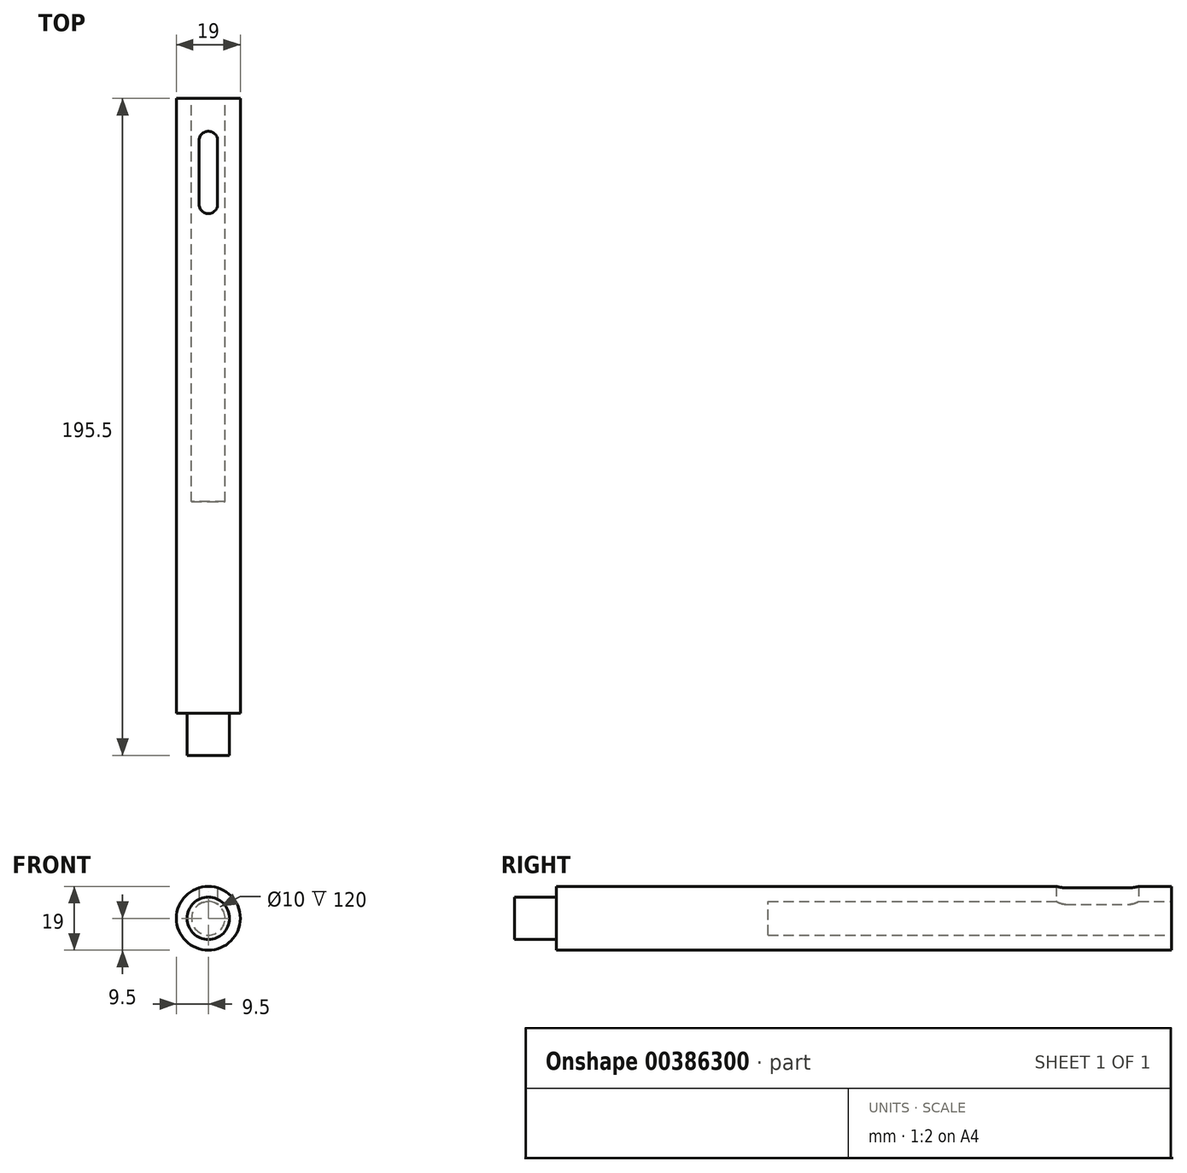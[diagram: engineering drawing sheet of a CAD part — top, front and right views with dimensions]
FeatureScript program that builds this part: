
annotation { "Feature Type Name" : "Feature", "Feature Type Description" : "" }
export const myFeature = defineFeature(function(context is Context, id is Id, definition is map)
    precondition{}
    {
        {
            var Q0;
            Q0=qCreatedBy(makeId("Front.planeOp"),FACE);
            var sketch = newSketch(context, id + "F0", { "sketchPlane" : qUnion([Q0])});
            skCircle(sketch, "E0", {"center": v(0, 0) * mm, "radius": 9.5 * mm});
            skCircle(sketch, "E1", {"center": v(0, 0) * mm, "radius": 5 * mm});
            skLineSegment(sketch, "E2", {"start": v(0, 20.65) * mm, "end": v(0, -19.38) * mm});
            skSolve(sketch);
        }
        {
            var Q0;
            {var subQ0=sQuery(id+"F0.wireOp",EDGE,"E2");var subQ1=sQuery(id+"F0.wireOp",EDGE,"E0");var subQ2=makeQuery(id+"F0.imprint","INTERSECT",VERTEX,{"disambiguationData":[OD(0.0)],"derivedFrom":[subQ1,subQ0]});Q0=makeQuery(id+"F0.imprint","IMPRINT",FACE,{"disambiguationData":[TD([[makeQuery(id+"F0.imprint","IMPRINT",EDGE,{"disambiguationData":[TD([[subQ2,-1.0]])],"derivedFrom":subQ1}),1.0]])]});}
            var Q1;
            {var subQ0=sQuery(id+"F0.wireOp",EDGE,"E2");var subQ1=sQuery(id+"F0.wireOp",EDGE,"E1");var subQ2=makeQuery(id+"F0.imprint","INTERSECT",VERTEX,{"disambiguationData":[OD(0.0)],"derivedFrom":[subQ1,subQ0]});Q1=makeQuery(id+"F0.imprint","IMPRINT",FACE,{"disambiguationData":[TD([[makeQuery(id+"F0.imprint","IMPRINT",EDGE,{"disambiguationData":[TD([[subQ2,-1.0]])],"derivedFrom":subQ1}),1.0]])]});}
            var Q2;
            {var subQ0=sQuery(id+"F0.wireOp",EDGE,"E2");var subQ1=sQuery(id+"F0.wireOp",EDGE,"E1");var subQ2=makeQuery(id+"F0.imprint","INTERSECT",VERTEX,{"disambiguationData":[OD(0.0)],"derivedFrom":[subQ1,subQ0]});Q2=makeQuery(id+"F0.imprint","IMPRINT",FACE,{"disambiguationData":[TD([[makeQuery(id+"F0.imprint","IMPRINT",EDGE,{"disambiguationData":[TD([[subQ2,1.0]])],"derivedFrom":subQ1}),1.0]])]});}
            var Q3;
            {var subQ0=sQuery(id+"F0.wireOp",EDGE,"E2");var subQ1=sQuery(id+"F0.wireOp",EDGE,"E0");var subQ2=makeQuery(id+"F0.imprint","INTERSECT",VERTEX,{"disambiguationData":[OD(0.0)],"derivedFrom":[subQ1,subQ0]});Q3=makeQuery(id+"F0.imprint","IMPRINT",FACE,{"disambiguationData":[TD([[makeQuery(id+"F0.imprint","IMPRINT",EDGE,{"disambiguationData":[TD([[subQ2,1.0]])],"derivedFrom":subQ1}),1.0]])]});}
            extrude(context, id + "F1", {"entities" : qUnion([Q0, Q1, Q2, Q3]), "depth" : 183 * mm});
        }
        {
            var Q0;
            {var subQ0=sQuery(id+"F0.wireOp",EDGE,"E2");var subQ1=sQuery(id+"F0.wireOp",EDGE,"E1");var subQ2=makeQuery(id+"F0.imprint","INTERSECT",VERTEX,{"disambiguationData":[OD(0.0)],"derivedFrom":[subQ1,subQ0]});Q0=makeQuery(id+"F0.imprint","IMPRINT",FACE,{"disambiguationData":[TD([[makeQuery(id+"F0.imprint","IMPRINT",EDGE,{"disambiguationData":[TD([[subQ2,-1.0]])],"derivedFrom":subQ1}),1.0]])]});}
            var Q1;
            {var subQ0=sQuery(id+"F0.wireOp",EDGE,"E2");var subQ1=sQuery(id+"F0.wireOp",EDGE,"E1");var subQ2=makeQuery(id+"F0.imprint","INTERSECT",VERTEX,{"disambiguationData":[OD(0.0)],"derivedFrom":[subQ1,subQ0]});Q1=makeQuery(id+"F0.imprint","IMPRINT",FACE,{"disambiguationData":[TD([[makeQuery(id+"F0.imprint","IMPRINT",EDGE,{"disambiguationData":[TD([[subQ2,1.0]])],"derivedFrom":subQ1}),1.0]])]});}
            extrude(context, id + "F2", {"entities" : qUnion([Q0, Q1]), "operationType" : NewBodyOperationType.REMOVE, "depth" : 120 * mm});
        }
        {
            var Q0;
            Q0=qCreatedBy(makeId("Top.planeOp"),FACE);
            var sketch = newSketch(context, id + "F3", { "sketchPlane" : qUnion([Q0])});
            skArc(sketch, "E3", {"start": v(2.75, -12.5) * mm, "mid": v(0, -9.75) * mm, "end": v(-2.75, -12.5) * mm});
            skArc(sketch, "E4", {"start": v(-2.75, -31.5) * mm, "mid": v(0, -34.25) * mm, "end": v(2.75, -31.5) * mm});
            skLineSegment(sketch, "E5", {"start": v(2.75, -12.5) * mm, "end": v(2.75, -31.5) * mm});
            skLineSegment(sketch, "E6", {"start": v(-2.75, -12.5) * mm, "end": v(-2.75, -31.5) * mm});
            skSolve(sketch);
        }
        {
            var Q0;
            Q0=qSketchRegion(id+"F3",true);
            extrude(context, id + "F4", {"entities" : qUnion([Q0]), "operationType" : NewBodyOperationType.REMOVE, "depth" : 25 * mm});
        }
        {
            var Q0;
            Q0=makeQuery(id+"F1.opExtrude","CAP_FACE",FACE,{"disambiguationData":[OSD([sQuery(id+"F0.wireOp",EDGE,"E0")])],"isStart":false});
            var sketch = newSketch(context, id + "F5", { "sketchPlane" : qUnion([Q0])});
            skCircle(sketch, "E7", {"center": v(0, 0) * mm, "radius": 6.3 * mm});
            skSolve(sketch);
        }
        {
            var Q0;
            Q0=makeQuery(id+"F5.imprint","IMPRINT",FACE,{"disambiguationData":[TD([[makeQuery(id+"F5.imprint","IMPRINT",EDGE,{"derivedFrom":sQuery(id+"F5.wireOp",EDGE,"E7")}),1.0]])]});
            extrude(context, id + "F6", {"entities" : qUnion([Q0]), "operationType" : NewBodyOperationType.ADD, "depth" : 12.5 * mm});
        }
    });
